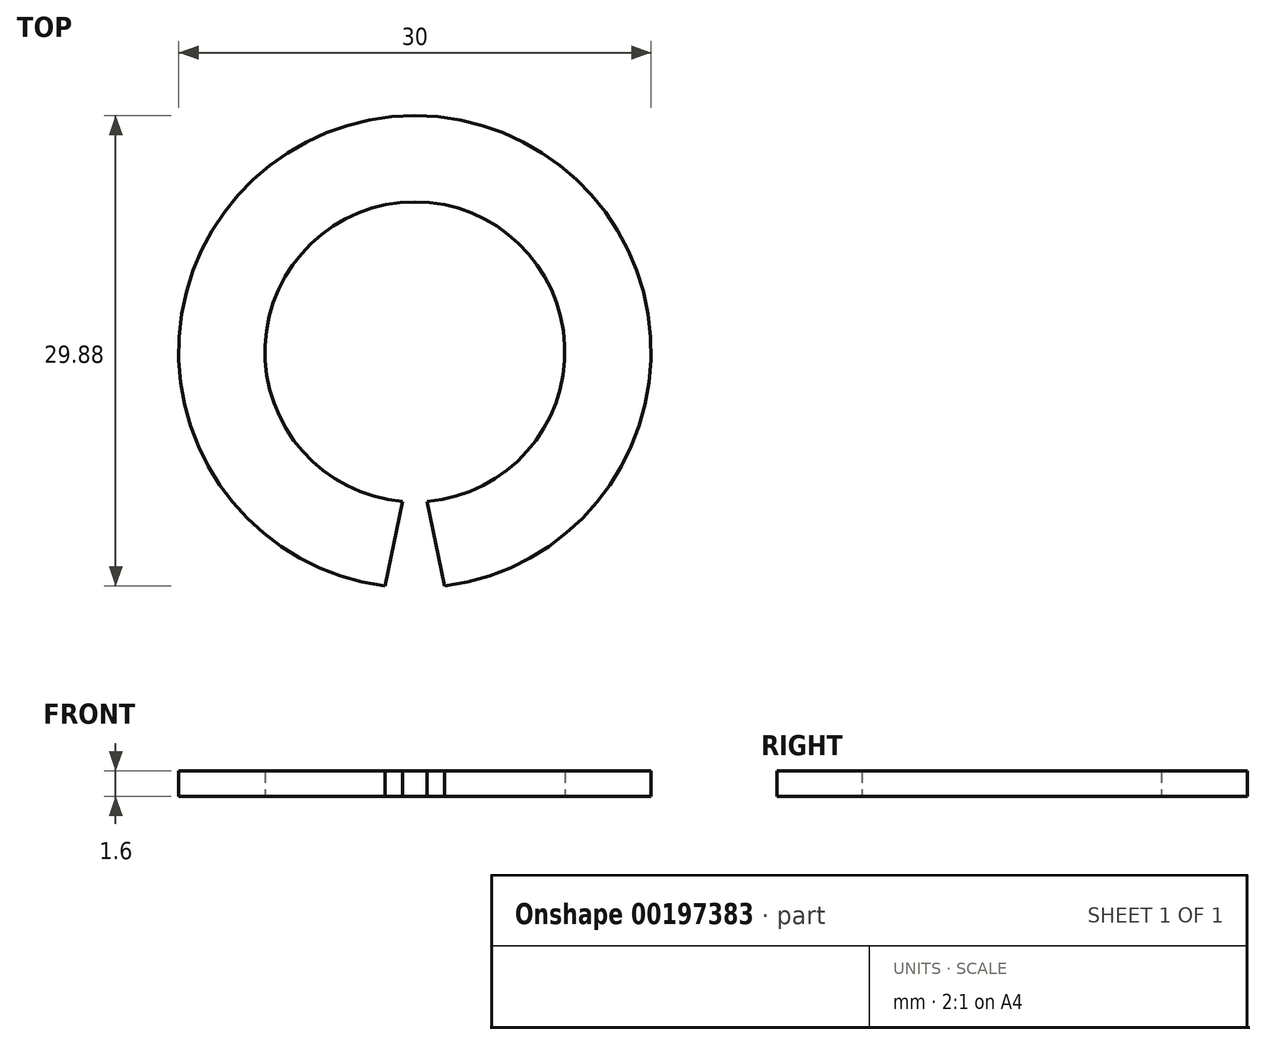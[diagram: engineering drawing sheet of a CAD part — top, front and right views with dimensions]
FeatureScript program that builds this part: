
annotation { "Feature Type Name" : "Feature", "Feature Type Description" : "" }
export const myFeature = defineFeature(function(context is Context, id is Id, definition is map)
    precondition{}
    {
        {
            var Q0;
            Q0=qCreatedBy(makeId("Top.planeOp"),FACE);
            var sketch = newSketch(context, id + "F0", { "sketchPlane" : qUnion([Q0])});
            skArc(sketch, "E0", {"start": v(0.77, -9.5) * mm, "mid": v(0, 9.53) * mm, "end": v(-0.77, -9.5) * mm});
            skArc(sketch, "E1", {"start": v(1.9, -14.88) * mm, "mid": v(0, 15) * mm, "end": v(-1.9, -14.88) * mm});
            skLineSegment(sketch, "E2", {"start": v(-0.77, -9.5) * mm, "end": v(-1.9, -14.88) * mm});
            skLineSegment(sketch, "E3.MirrorCS", {"start": v(0.77, -9.5) * mm, "end": v(1.9, -14.88) * mm});
            skSolve(sketch);
        }
        {
            var Q0;
            Q0=qSketchRegion(id+"F0",true);
            extrude(context, id + "F1", {"entities" : qUnion([Q0]), "endBound" : BoundingType.SYMMETRIC, "depth" : 1.6 * mm});
        }
    });
